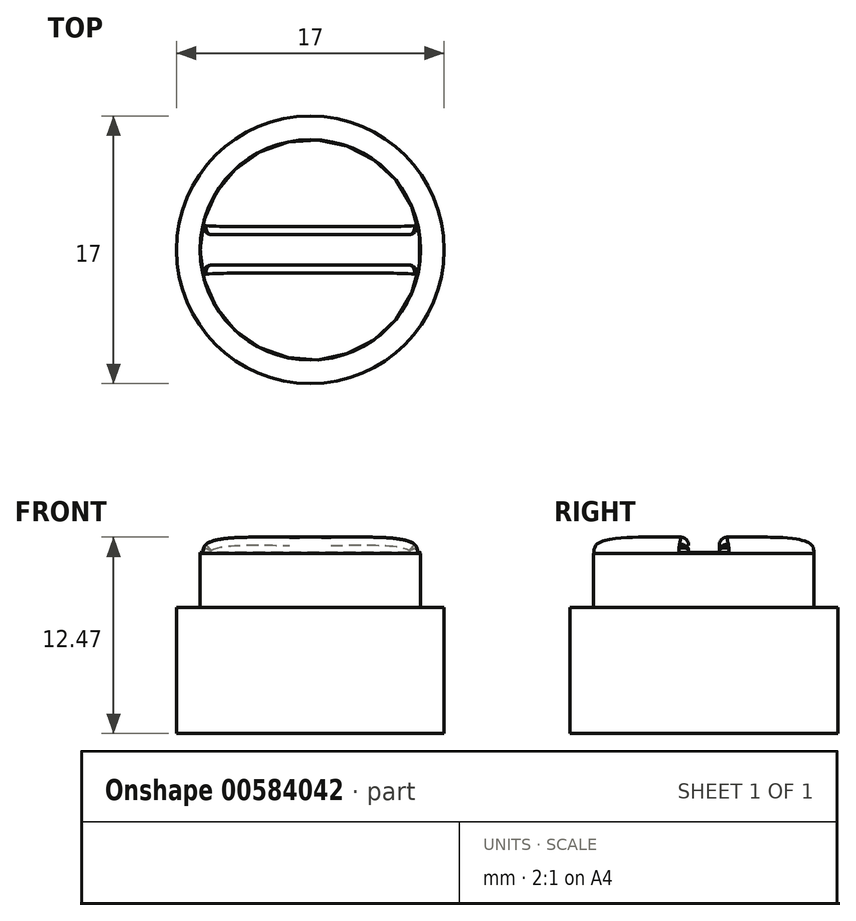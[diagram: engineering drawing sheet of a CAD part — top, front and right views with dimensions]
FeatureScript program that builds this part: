
annotation { "Feature Type Name" : "Feature", "Feature Type Description" : "" }
export const myFeature = defineFeature(function(context is Context, id is Id, definition is map)
    precondition{}
    {
        {
            var Q0;
            Q0=qCreatedBy(makeId("Top.planeOp"),FACE);
            var sketch = newSketch(context, id + "F0", { "sketchPlane" : qUnion([Q0])});
            skCircle(sketch, "E0", {"center": v(0, 0) * mm, "radius": 7 * mm});
            skCircle(sketch, "E1", {"center": v(0, 0) * mm, "radius": 8.5 * mm});
            skSolve(sketch);
        }
        {
            var Q0;
            Q0=makeQuery(id+"F0.imprint","IMPRINT",FACE,{"disambiguationData":[TD([[makeQuery(id+"F0.imprint","IMPRINT",EDGE,{"derivedFrom":sQuery(id+"F0.wireOp",EDGE,"E0")}),1.0]])]});
            extrude(context, id + "F1", {"entities" : qUnion([Q0]), "depth" : 12.5 * mm, "offsetDistance" : 25 * mm});
        }
        {
            var Q0;
            Q0=qSketchRegion(id+"F0",true);
            extrude(context, id + "F2", {"entities" : qUnion([Q0]), "operationType" : NewBodyOperationType.ADD, "depth" : 8 * mm, "offsetDistance" : 25 * mm});
        }
        {
            var Q0;
            Q0=makeQuery(id+"F1.opExtrude","CAP_FACE",FACE,{"disambiguationData":[OSD([sQuery(id+"F0.wireOp",EDGE,"E0")])],"isStart":false});
            var sketch = newSketch(context, id + "F3", { "sketchPlane" : qUnion([Q0])});
            skPoint(sketch, "E2.middle", {"position": v(0.25, 0) * mm});
            skLineSegment(sketch, "E3.bottom", {"start": v(8.6, -0.97) * mm, "end": v(-8.1, -0.97) * mm});
            skLineSegment(sketch, "E3.top", {"start": v(8.6, 0.97) * mm, "end": v(-8.1, 0.97) * mm});
            skLineSegment(sketch, "E3.left", {"start": v(8.6, -0.97) * mm, "end": v(8.6, 0.97) * mm});
            skLineSegment(sketch, "E3.right", {"start": v(-8.1, -0.97) * mm, "end": v(-8.1, 0.97) * mm});
            skSolve(sketch);
        }
        {
            var Q0;
            Q0=qCreatedBy(makeId("Front.planeOp"),FACE);
            var sketch = newSketch(context, id + "F4", { "sketchPlane" : qUnion([Q0])});
            skFitSpline(sketch, "E4", {"points": [v(0, 12.5) * mm, v(-4.49, 12.46) * mm, v(-6.87, 11.93) * mm, v(-6.99, 11.46) * mm, v(-7, 11.41) * mm], "startDerivative": vector(-10.92, -0.71) * mm, "endDerivative": vector(-0.37, -0.56) * mm});
            skFitSpline(sketch, "E5", {"points": [v(-1.68, 12.39) * mm, v(-1.96, 12.45) * mm], "startDerivative": vector(-0.02, 0.02) * mm, "endDerivative": vector(-0.16, 0.2) * mm});
            skLineSegment(sketch, "E6", {"start": v(-7, 11.42) * mm, "end": v(-8.48, 11.42) * mm});
            skLineSegment(sketch, "E7", {"start": v(-8.48, 11.42) * mm, "end": v(-8.48, 12.95) * mm});
            skLineSegment(sketch, "E8", {"start": v(-8.48, 12.95) * mm, "end": v(0, 12.95) * mm});
            skLineSegment(sketch, "E9", {"start": v(0, 12.95) * mm, "end": v(0, 12.5) * mm, "construction": true});
            skLineSegment(sketch, "E10", {"start": v(-8.48, 11.62) * mm, "end": v(0, 11.62) * mm, "construction": true});
            skLineSegment(sketch, "E11", {"start": v(0, 12.95) * mm, "end": v(0, 12.5) * mm});
            skSolve(sketch);
        }
        {
            var Q0;
            Q0=makeQuery(id+"F4.imprint","IMPRINT",FACE,{"disambiguationData":[TD([[makeQuery(id+"F4.imprint","IMPRINT",EDGE,{"derivedFrom":sQuery(id+"F4.wireOp",EDGE,"ac4bd4f6-319e-4e15-baa9-e55c222e8029")}),-1.0]])]});
            var Q1;
            {var subQ0=sQuery(id+"F4.wireOp",EDGE,"E7");Q1=makeQuery(id+"F4.imprint","IMPRINT",FACE,{"disambiguationData":[TD([[makeQuery(id+"F4.imprint","IMPRINT",EDGE,{"derivedFrom":subQ0}),-1.0]])]});}
            var Q2;
            Q2=sQuery(id+"F4.wireOp",EDGE,"E11");
            revolve(context, id + "F5", {"operationType" : NewBodyOperationType.REMOVE, "entities" : qUnion([Q0, Q1]), "axis" : qUnion([Q2]), "revolveType" : RevolveType.FULL, "oppositeDirection" : true});
        }
        {
            var Q0;
            {var subQ0=sQuery(id+"F3.wireOp",EDGE,"bd7cf013-96ed-46fa-b71a-ad90aaa50927.sketch_text.stroke-7");Q0=makeQuery(id+"F3.imprint","IMPRINT",FACE,{"disambiguationData":[TD([[makeQuery(id+"F3.imprint","IMPRINT",EDGE,{"derivedFrom":subQ0}),-1.0]])]});}
            var Q1;
            {var subQ0=sQuery(id+"F3.wireOp",EDGE,"bd7cf013-96ed-46fa-b71a-ad90aaa50927.sketch_text.stroke-1");Q1=makeQuery(id+"F3.imprint","IMPRINT",FACE,{"disambiguationData":[TD([[makeQuery(id+"F3.imprint","IMPRINT",EDGE,{"derivedFrom":subQ0}),-1.0]])]});}
            var Q2;
            {var subQ0=sQuery(id+"F3.wireOp",EDGE,"bd7cf013-96ed-46fa-b71a-ad90aaa50927.sketch_text.stroke-4");Q2=makeQuery(id+"F3.imprint","IMPRINT",FACE,{"disambiguationData":[TD([[makeQuery(id+"F3.imprint","IMPRINT",EDGE,{"derivedFrom":subQ0}),-1.0]])]});}
            var Q3;
            Q3=qSketchRegion(id+"F3",true);
            extrude(context, id + "F6", {"entities" : qUnion([Q0, Q1, Q2, Q3]), "operationType" : NewBodyOperationType.REMOVE, "oppositeDirection" : true, "depth" : 1 * mm, "offsetDistance" : 25 * mm});
        }
        {
            var Q0;
            Q0=makeQuery(id+"F6.boolean.opBoolean","INTERSECT",EDGE,{"derivedFrom":[makeQuery(id+"F5.boolean.opBoolean","COPY",FACE,{"derivedFrom":makeQuery(id+"F5.opRevolve","SWEPT_FACE",FACE,{"disambiguationData":[OSD([sQuery(id+"F4.wireOp",EDGE,"E4")])]})}),makeQuery(id+"F6.opExtrude","SWEPT_FACE",FACE,{"disambiguationData":[OSD([sQuery(id+"F3.wireOp",EDGE,"E3.top")])]})]});
            var Q1;
            Q1=makeQuery(id+"F6.boolean.opBoolean","INTERSECT",EDGE,{"derivedFrom":[makeQuery(id+"F5.boolean.opBoolean","COPY",FACE,{"derivedFrom":makeQuery(id+"F5.opRevolve","SWEPT_FACE",FACE,{"disambiguationData":[OSD([sQuery(id+"F4.wireOp",EDGE,"E4")])]})}),makeQuery(id+"F6.opExtrude","SWEPT_FACE",FACE,{"disambiguationData":[OSD([sQuery(id+"F3.wireOp",EDGE,"E3.bottom")])]})]});
            fillet(context, id + "F7", {"entities" : qUnion([Q0, Q1]), "radius" : .5 * mm, "tangentPropagation" : true, "allowEdgeOverflow" : false});
        }
    });
